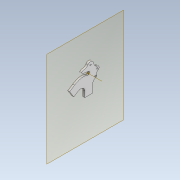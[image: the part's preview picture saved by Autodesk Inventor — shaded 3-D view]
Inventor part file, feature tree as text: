
AUTODESK INVENTOR PART (.ipt)
format: ipt  version: 2021 (Build 250183000, 183)  size: 166,400 bytes
history: native  units: mm
features: other x9, reference x6, sketch x2, plane x1, extrude x1, hole x1
ambient origin geometry x8: Origin, YZ Plane, XZ Plane, XY Plane, X Axis, Y Axis, Z Axis, Center Point
bodies: Body1 (feature_tree)
feature tree (20):
  other  "Sólido1"
  plane  "Plano de trabajo1"
  extrude  "Extrusión1"  TaperAngle=60.0deg  [1 undecoded]
  hole  "Agujero1"  [1 undecoded]
  other  "Punto de trabajo1"
  sketch  "Boceto1"  dims[d75=20.0mm d76=60.0deg]
  reference  "Referencia1"
  reference  "Referencia2"
  reference  "Referencia3"
  reference  "Referencia4"
  reference  "Referencia5"
  reference  "Referencia6"
  sketch  "Boceto2"  dims[d77=15.0mm d78=8.0mm d232=15.0mm d233=10.0mm d234=8.0mm d286=5.0mm d287=0.0mm d290=0.349066mm d291=50.0mm d292=3.4mm d293=6.0mm d294=6.3mm d295=2.0mm d296=90.0deg d297=8.0mm d298=20.594885mm]
  other  "Eje de trabajo1"
  parser-record x1  (decoder bookkeeping rows leaked as tree rows — omitted from the tree; the rows remain in map.json)
  other  "Marco_Bicicleta.iam"
  other  "Esqueleto_estructura:1"
  other  "Estructura 1617045494032:1"
  other  "ANSI  1617061874634:1"
  other  "ANSI  1618003984630:1"
note: 2 required parameter values undecoded (feature->parameter linkage not recoverable at this tier; creation-order binding heuristic only, values carry confidence <= 0.55)
note: 1 file-system path scrubbed to <path> (originals preserved in map.json)
